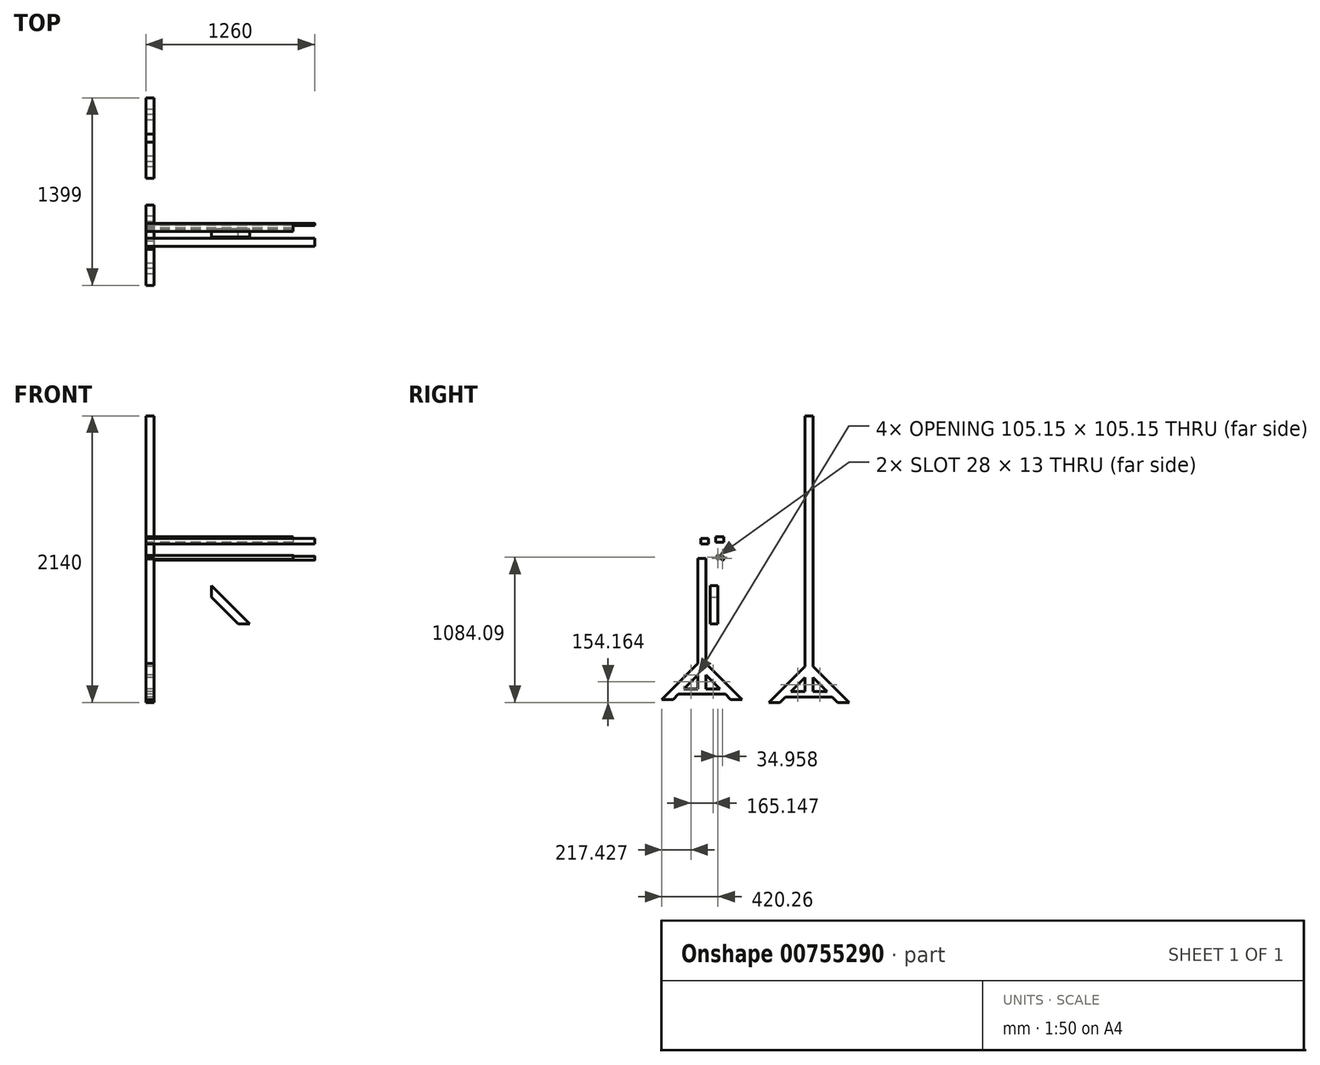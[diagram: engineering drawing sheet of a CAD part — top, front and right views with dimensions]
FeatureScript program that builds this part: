
annotation { "Feature Type Name" : "Feature", "Feature Type Description" : "" }
export const myFeature = defineFeature(function(context is Context, id is Id, definition is map)
    precondition{}
    {
        {
            var Q0;
            Q0=qCreatedBy(makeId("Right.planeOp"),FACE);
            var sketch = newSketch(context, id + "F0", { "sketchPlane" : qUnion([Q0])});
            skLineSegment(sketch, "E0", {"start": v(-7.5, 0) * mm, "end": v(-7.5, 15) * mm});
            skLineSegment(sketch, "E1", {"start": v(7.5, 0) * mm, "end": v(7.5, 15) * mm});
            skLineSegment(sketch, "E2", {"start": v(-7.5, 0) * mm, "end": v(7.5, 0) * mm, "construction": true});
            skArc(sketch, "E3", {"start": v(-7.5, 15) * mm, "mid": v(0, 22.5) * mm, "end": v(7.5, 15) * mm});
            skArc(sketch, "E4", {"start": v(7.5, 0) * mm, "mid": v(0, -7.5) * mm, "end": v(-7.5, 0) * mm});
            skLineSegment(sketch, "E5", {"start": v(-6.5, 0) * mm, "end": v(-6.5, 15) * mm});
            skLineSegment(sketch, "E6", {"start": v(6.5, 15) * mm, "end": v(6.5, 0) * mm});
            skLineSegment(sketch, "E7", {"start": v(-6.5, 15) * mm, "end": v(6.5, 15) * mm, "construction": true});
            skArc(sketch, "E8", {"start": v(-6.5, 15) * mm, "mid": v(0, 21.5) * mm, "end": v(6.5, 15) * mm});
            skArc(sketch, "E9", {"start": v(6.5, 0) * mm, "mid": v(0, -6.5) * mm, "end": v(-6.5, 0) * mm});
            skSolve(sketch);
        }
        {
            var Q0;
            Q0 = qSketchRegion(id + "F0", true);
            extrude(context, id + "F1", {"entities" : qUnion([Q0]), "depth" : 1100 * mm, "offsetDistance" : 25 * mm});
        }
        {
            var Q0;
            Q0=qCreatedBy(makeId("Right.planeOp"),FACE);
            var sketch = newSketch(context, id + "F2", { "sketchPlane" : qUnion([Q0])});
            skLineSegment(sketch, "E10", {"start": v(-90.26, 0) * mm, "end": v(-90.26, -785) * mm});
            skLineSegment(sketch, "E11", {"start": v(-90.26, -785) * mm, "end": v(179.74, -1055) * mm});
            skLineSegment(sketch, "E12", {"start": v(179.74, -1055) * mm, "end": v(94.89, -1055) * mm});
            skLineSegment(sketch, "E13", {"start": v(94.89, -1055) * mm, "end": v(54.89, -1015) * mm});
            skLineSegment(sketch, "E14", {"start": v(54.89, -1015) * mm, "end": v(-295.4, -1015) * mm});
            skLineSegment(sketch, "E15", {"start": v(-295.4, -1015) * mm, "end": v(-335.4, -1055) * mm});
            skLineSegment(sketch, "E16", {"start": v(-335.4, -1055) * mm, "end": v(-420.26, -1055) * mm});
            skLineSegment(sketch, "E17", {"start": v(-420.26, -1055) * mm, "end": v(-150.26, -785) * mm});
            skLineSegment(sketch, "E18", {"start": v(-150.26, -785) * mm, "end": v(-150.26, 0) * mm});
            skLineSegment(sketch, "E19", {"start": v(-150.26, 0) * mm, "end": v(-90.26, 0) * mm});
            skLineSegment(sketch, "E20", {"start": v(-90.26, -869.85) * mm, "end": v(-90.26, -975) * mm});
            skLineSegment(sketch, "E21", {"start": v(-90.26, -975) * mm, "end": v(14.89, -975) * mm});
            skLineSegment(sketch, "E22", {"start": v(14.89, -975) * mm, "end": v(-90.26, -869.85) * mm});
            skLineSegment(sketch, "E23", {"start": v(-150.26, -869.85) * mm, "end": v(-150.26, -975) * mm});
            skLineSegment(sketch, "E24", {"start": v(-150.26, -975) * mm, "end": v(-255.4, -975) * mm});
            skLineSegment(sketch, "E25", {"start": v(-255.4, -975) * mm, "end": v(-150.26, -869.85) * mm});
            skLineSegment(sketch, "E26", {"start": v(-255.4, -975) * mm, "end": v(-295.4, -1015) * mm, "construction": true});
            skLineSegment(sketch, "E27", {"start": v(14.89, -975) * mm, "end": v(54.89, -1015) * mm, "construction": true});
            skLineSegment(sketch, "E28", {"start": v(-90.26, -975) * mm, "end": v(-150.26, -975) * mm, "construction": true});
            skLineSegment(sketch, "E29", {"start": v(-90.26, -785) * mm, "end": v(-90.26, -869.85) * mm, "construction": true});
            skLineSegment(sketch, "E30", {"start": v(-150.26, -785) * mm, "end": v(-150.26, -869.85) * mm, "construction": true});
            skLineSegment(sketch, "E31", {"start": v(-90.26, -40) * mm, "end": v(-150.26, -40) * mm, "construction": true});
            skLineSegment(sketch, "E32", {"start": v(-90.26, -45) * mm, "end": v(-150.26, -45) * mm, "construction": true});
            skLineSegment(sketch, "E33", {"start": v(-90.26, -75) * mm, "end": v(-150.26, -75) * mm, "construction": true});
            skSolve(sketch);
        }
        {
            var Q0;
            Q0=qCreatedBy(makeId("Right.planeOp"),FACE);
            var sketch = newSketch(context, id + "F3", { "sketchPlane" : qUnion([Q0])});
            skLineSegment(sketch, "E34", {"start": v(708.74, -21.59) * mm, "end": v(708.74, -806.59) * mm});
            skLineSegment(sketch, "E35", {"start": v(708.74, -806.59) * mm, "end": v(978.74, -1076.59) * mm});
            skLineSegment(sketch, "E36", {"start": v(978.74, -1076.59) * mm, "end": v(893.88, -1076.59) * mm});
            skLineSegment(sketch, "E37", {"start": v(893.88, -1076.59) * mm, "end": v(853.88, -1036.59) * mm});
            skLineSegment(sketch, "E38", {"start": v(853.88, -1036.59) * mm, "end": v(503.59, -1036.59) * mm});
            skLineSegment(sketch, "E39", {"start": v(503.59, -1036.59) * mm, "end": v(463.59, -1076.59) * mm});
            skLineSegment(sketch, "E40", {"start": v(463.59, -1076.59) * mm, "end": v(378.74, -1076.59) * mm});
            skLineSegment(sketch, "E41", {"start": v(378.74, -1076.59) * mm, "end": v(648.74, -806.59) * mm});
            skLineSegment(sketch, "E42", {"start": v(648.74, -806.59) * mm, "end": v(648.74, -21.59) * mm});
            skLineSegment(sketch, "E43", {"start": v(648.74, -21.59) * mm, "end": v(708.74, -21.59) * mm, "construction": true});
            skLineSegment(sketch, "E44", {"start": v(708.74, -891.44) * mm, "end": v(708.74, -996.59) * mm});
            skLineSegment(sketch, "E45", {"start": v(708.74, -996.59) * mm, "end": v(813.88, -996.59) * mm});
            skLineSegment(sketch, "E46", {"start": v(813.88, -996.59) * mm, "end": v(708.74, -891.44) * mm});
            skLineSegment(sketch, "E47", {"start": v(648.74, -891.44) * mm, "end": v(648.74, -996.59) * mm});
            skLineSegment(sketch, "E48", {"start": v(648.74, -996.59) * mm, "end": v(543.59, -996.59) * mm});
            skLineSegment(sketch, "E49", {"start": v(543.59, -996.59) * mm, "end": v(648.74, -891.44) * mm});
            skLineSegment(sketch, "E50", {"start": v(543.59, -996.59) * mm, "end": v(503.59, -1036.59) * mm, "construction": true});
            skLineSegment(sketch, "E51", {"start": v(813.88, -996.59) * mm, "end": v(853.88, -1036.59) * mm, "construction": true});
            skLineSegment(sketch, "E52", {"start": v(708.74, -996.59) * mm, "end": v(648.74, -996.59) * mm, "construction": true});
            skLineSegment(sketch, "E53", {"start": v(708.74, -806.59) * mm, "end": v(708.74, -891.44) * mm, "construction": true});
            skLineSegment(sketch, "E54", {"start": v(648.74, -806.59) * mm, "end": v(648.74, -891.44) * mm, "construction": true});
            skLineSegment(sketch, "E55", {"start": v(708.74, -61.59) * mm, "end": v(648.74, -61.59) * mm, "construction": true});
            skLineSegment(sketch, "E56", {"start": v(708.74, -66.59) * mm, "end": v(648.74, -66.59) * mm, "construction": true});
            skLineSegment(sketch, "E57", {"start": v(708.74, -96.59) * mm, "end": v(648.74, -96.59) * mm, "construction": true});
            skLineSegment(sketch, "E58", {"start": v(708.74, -21.59) * mm, "end": v(708.74, 1063.41) * mm});
            skLineSegment(sketch, "E59", {"start": v(708.74, 1063.41) * mm, "end": v(648.74, 1063.41) * mm});
            skLineSegment(sketch, "E60", {"start": v(648.74, 1063.41) * mm, "end": v(648.74, -21.59) * mm});
            skLineSegment(sketch, "E61", {"start": v(708.74, 1023.41) * mm, "end": v(648.74, 1023.41) * mm, "construction": true});
            skLineSegment(sketch, "E62", {"start": v(708.74, 1018.41) * mm, "end": v(648.74, 1018.41) * mm, "construction": true});
            skLineSegment(sketch, "E63", {"start": v(708.74, 988.41) * mm, "end": v(648.74, 988.41) * mm, "construction": true});
            skLineSegment(sketch, "E64", {"start": v(708.74, 48.41) * mm, "end": v(648.74, 48.41) * mm, "construction": true});
            skLineSegment(sketch, "E65", {"start": v(708.74, 88.41) * mm, "end": v(648.74, 88.41) * mm, "construction": true});
            skSolve(sketch);
        }
        {
            var Q0;
            Q0 = qSketchRegion(id + "F2", true);
            var Q1;
            Q1 = qSketchRegion(id + "F3", true);
            extrude(context, id + "F4", {"entities" : qUnion([Q0, Q1]), "depth" : 60 * mm, "offsetDistance" : 25 * mm});
        }
        {
            var Q0;
            Q0=qCreatedBy(makeId("Right.planeOp"),FACE);
            var sketch = newSketch(context, id + "F5", { "sketchPlane" : qUnion([Q0])});
            skLineSegment(sketch, "E66", {"start": v(27.46, -7.5) * mm, "end": v(27.46, 7.5) * mm});
            skLineSegment(sketch, "E67", {"start": v(42.46, -7.5) * mm, "end": v(42.46, 7.5) * mm});
            skLineSegment(sketch, "E68", {"start": v(27.46, -7.5) * mm, "end": v(42.46, -7.5) * mm, "construction": true});
            skArc(sketch, "E69", {"start": v(27.46, 7.5) * mm, "mid": v(34.96, 15) * mm, "end": v(42.46, 7.5) * mm});
            skArc(sketch, "E70", {"start": v(42.46, -7.5) * mm, "mid": v(34.96, -15) * mm, "end": v(27.46, -7.5) * mm});
            skLineSegment(sketch, "E71", {"start": v(28.46, -7.5) * mm, "end": v(28.46, 7.5) * mm});
            skLineSegment(sketch, "E72", {"start": v(41.46, 7.5) * mm, "end": v(41.46, -7.5) * mm});
            skLineSegment(sketch, "E73", {"start": v(28.46, 7.5) * mm, "end": v(41.46, 7.5) * mm, "construction": true});
            skArc(sketch, "E74", {"start": v(28.46, 7.5) * mm, "mid": v(34.96, 14) * mm, "end": v(41.46, 7.5) * mm});
            skArc(sketch, "E75", {"start": v(41.46, -7.5) * mm, "mid": v(34.96, -14) * mm, "end": v(28.46, -7.5) * mm});
            skSolve(sketch);
        }
        {
            var Q0;
            Q0 = qSketchRegion(id + "F5", true);
            extrude(context, id + "F6", {"entities" : qUnion([Q0]), "depth" : 1260 * mm, "offsetDistance" : 25 * mm});
        }
        {
            var Q0;
            Q0=qCreatedBy(makeId("Right.planeOp"),FACE);
            var sketch = newSketch(context, id + "F7", { "sketchPlane" : qUnion([Q0])});
            skLineSegment(sketch, "E76.bottom", {"start": v(42.95, 160.24) * mm, "end": v(-17.05, 160.24) * mm});
            skLineSegment(sketch, "E76.top", {"start": v(42.95, 120.24) * mm, "end": v(-17.05, 120.24) * mm});
            skLineSegment(sketch, "E76.left", {"start": v(42.95, 160.24) * mm, "end": v(42.95, 120.24) * mm});
            skLineSegment(sketch, "E76.right", {"start": v(-17.05, 160.24) * mm, "end": v(-17.05, 120.24) * mm});
            skSolve(sketch);
        }
        {
            var Q0;
            Q0=qCreatedBy(makeId("Right.planeOp"),FACE);
            var sketch = newSketch(context, id + "F8", { "sketchPlane" : qUnion([Q0])});
            skLineSegment(sketch, "E77.bottom", {"start": v(-69.87, 147.75) * mm, "end": v(-129.87, 147.75) * mm});
            skLineSegment(sketch, "E77.top", {"start": v(-69.87, 107.75) * mm, "end": v(-129.87, 107.75) * mm});
            skLineSegment(sketch, "E77.left", {"start": v(-69.87, 147.75) * mm, "end": v(-69.87, 107.75) * mm});
            skLineSegment(sketch, "E77.right", {"start": v(-129.87, 147.75) * mm, "end": v(-129.87, 107.75) * mm});
            skSolve(sketch);
        }
        {
            var Q0;
            Q0 = qSketchRegion(id + "F7", true);
            extrude(context, id + "F9", {"entities" : qUnion([Q0]), "depth" : 1100 * mm, "offsetDistance" : 25 * mm});
        }
        {
            var Q0;
            Q0 = qSketchRegion(id + "F8", true);
            extrude(context, id + "F10", {"entities" : qUnion([Q0]), "depth" : 1260 * mm, "offsetDistance" : 25 * mm});
        }
        {
            var Q0;
            Q0=qCreatedBy(makeId("Front.planeOp"),FACE);
            var sketch = newSketch(context, id + "F11", { "sketchPlane" : qUnion([Q0])});
            skLineSegment(sketch, "E78", {"start": v(489.48, -204.94) * mm, "end": v(774.33, -489.8) * mm});
            skLineSegment(sketch, "E79", {"start": v(774.33, -489.8) * mm, "end": v(689.48, -489.8) * mm});
            skLineSegment(sketch, "E80", {"start": v(689.48, -489.8) * mm, "end": v(489.48, -289.8) * mm});
            skLineSegment(sketch, "E81", {"start": v(489.48, -289.8) * mm, "end": v(489.48, -204.94) * mm});
            skSolve(sketch);
        }
        {
            var Q0;
            Q0 = qSketchRegion(id + "F11", true);
            extrude(context, id + "F12", {"entities" : qUnion([Q0]), "depth" : 60 * mm, "offsetDistance" : 25 * mm});
        }
    });
